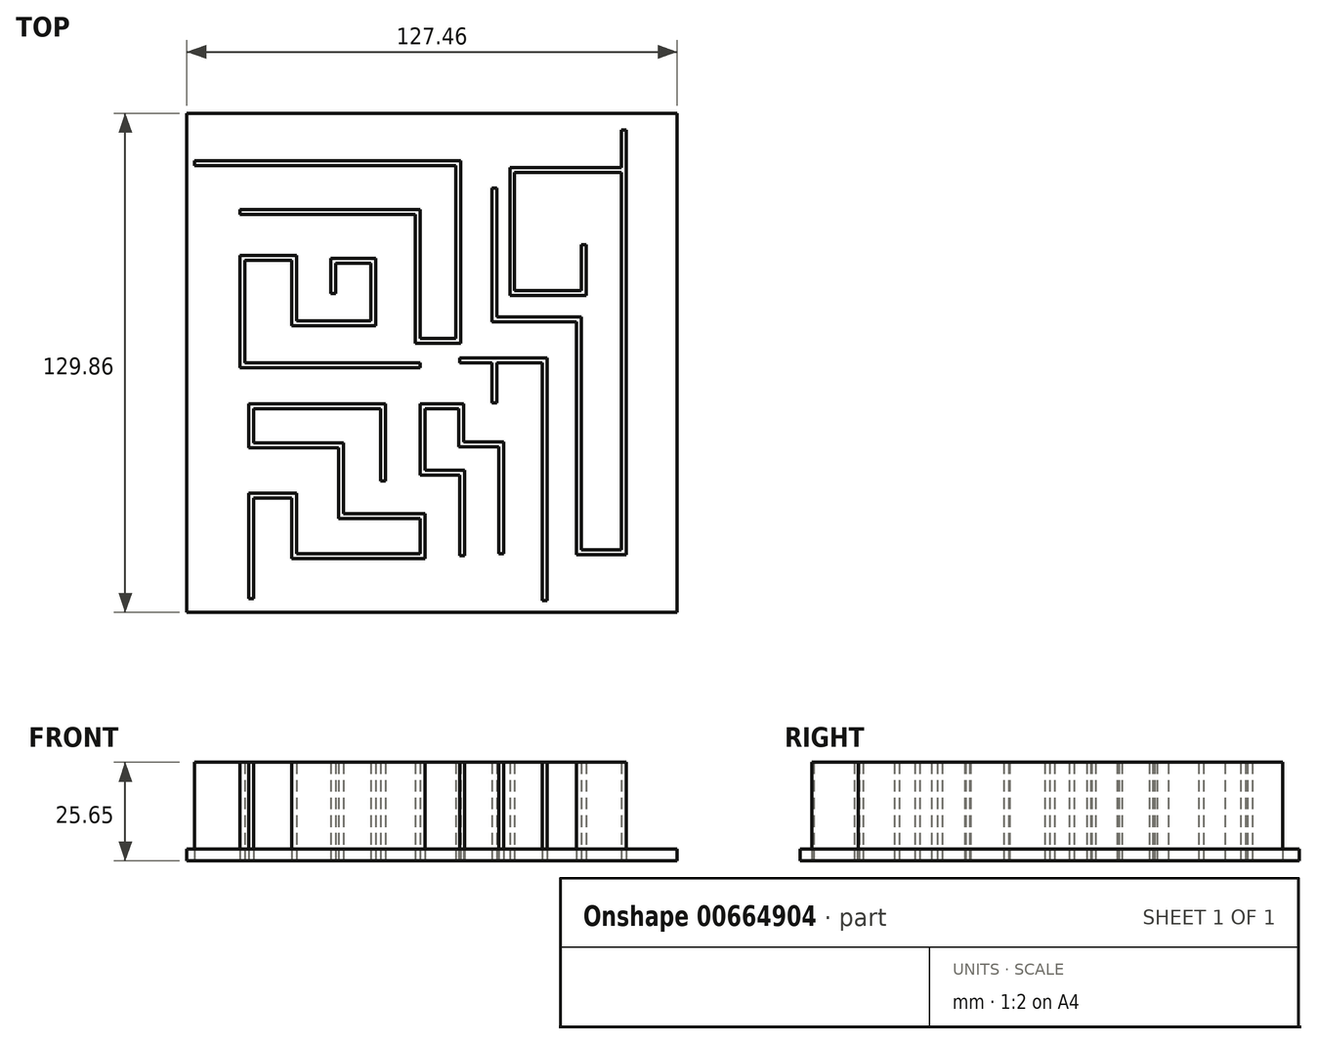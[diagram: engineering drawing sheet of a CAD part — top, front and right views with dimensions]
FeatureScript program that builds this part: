
annotation { "Feature Type Name" : "Feature", "Feature Type Description" : "" }
export const myFeature = defineFeature(function(context is Context, id is Id, definition is map)
    precondition{}
    {
        {
            var Q0;
            Q0=qCreatedBy(makeId("Top.planeOp"),FACE);
            var sketch = newSketch(context, id + "F0", { "sketchPlane" : qUnion([Q0])});
            skLineSegment(sketch, "E0", {"start": v(-44.65, -61.31) * mm, "end": v(-44.65, -33.84) * mm});
            skLineSegment(sketch, "E1", {"start": v(-44.65, -33.84) * mm, "end": v(-32.18, -33.84) * mm});
            skLineSegment(sketch, "E2", {"start": v(-32.18, -33.84) * mm, "end": v(-32.18, -49.6) * mm});
            skLineSegment(sketch, "E3", {"start": v(-32.18, -49.6) * mm, "end": v(0, -49.6) * mm});
            skLineSegment(sketch, "E4", {"start": v(0, -49.6) * mm, "end": v(0, -40.45) * mm});
            skLineSegment(sketch, "E5", {"start": v(0, -40.45) * mm, "end": v(-21.24, -40.45) * mm});
            skLineSegment(sketch, "E6", {"start": v(-21.24, -40.45) * mm, "end": v(-21.24, -22.13) * mm});
            skLineSegment(sketch, "E7", {"start": v(-21.24, -22.13) * mm, "end": v(-44.65, -22.13) * mm});
            skLineSegment(sketch, "E8", {"start": v(-44.65, -22.13) * mm, "end": v(-44.65, -10.68) * mm});
            skLineSegment(sketch, "E9", {"start": v(-44.65, -10.68) * mm, "end": v(-9.03, -10.68) * mm});
            skLineSegment(sketch, "E10", {"start": v(-9.03, -10.68) * mm, "end": v(-9.03, -30.78) * mm});
            skLineSegment(sketch, "E11", {"start": v(0, 0) * mm, "end": v(-45.67, 0) * mm});
            skLineSegment(sketch, "E12", {"start": v(-45.67, 0) * mm, "end": v(-45.67, 26.71) * mm});
            skLineSegment(sketch, "E13", {"start": v(-45.67, 26.71) * mm, "end": v(-33.45, 26.71) * mm});
            skLineSegment(sketch, "E14", {"start": v(-33.45, 26.71) * mm, "end": v(-33.45, 9.67) * mm});
            skLineSegment(sketch, "E15", {"start": v(-33.45, 9.67) * mm, "end": v(-11.58, 9.67) * mm});
            skLineSegment(sketch, "E16", {"start": v(-11.58, 9.67) * mm, "end": v(-11.58, 27.22) * mm});
            skLineSegment(sketch, "E17", {"start": v(-11.58, 27.22) * mm, "end": v(-23.28, 27.22) * mm});
            skLineSegment(sketch, "E18", {"start": v(-23.28, 27.22) * mm, "end": v(-23.28, 18.06) * mm});
            skLineSegment(sketch, "E19", {"start": v(0, 39.93) * mm, "end": v(0, 6.37) * mm});
            skLineSegment(sketch, "E20", {"start": v(0, 6.37) * mm, "end": v(9.29, 6.37) * mm});
            skLineSegment(sketch, "E21", {"start": v(9.29, 6.37) * mm, "end": v(9.29, 51.38) * mm});
            skLineSegment(sketch, "E22", {"start": v(9.29, 51.38) * mm, "end": v(-46.67, 51.38) * mm});
            skLineSegment(sketch, "E23", {"start": v(10.3, -50.12) * mm, "end": v(10.3, -29.26) * mm});
            skLineSegment(sketch, "E24", {"start": v(10.3, -29.26) * mm, "end": v(0, -29.26) * mm});
            skLineSegment(sketch, "E25", {"start": v(0, -29.26) * mm, "end": v(0, -10.68) * mm});
            skLineSegment(sketch, "E26", {"start": v(0, -10.68) * mm, "end": v(11.32, -10.68) * mm});
            skLineSegment(sketch, "E27", {"start": v(11.32, -10.68) * mm, "end": v(11.32, -20.6) * mm});
            skLineSegment(sketch, "E28", {"start": v(11.32, -20.6) * mm, "end": v(21.75, -20.6) * mm});
            skLineSegment(sketch, "E29", {"start": v(21.75, -20.6) * mm, "end": v(21.75, -49.6) * mm});
            skLineSegment(sketch, "E30", {"start": v(21.75, -49.6) * mm, "end": v(31.67, -49.6) * mm});
            skLineSegment(sketch, "E31", {"start": v(31.67, -49.6) * mm, "end": v(31.67, -10.44) * mm});
            skLineSegment(sketch, "E32", {"start": v(31.67, -10.44) * mm, "end": v(31.67, 0) * mm});
            skLineSegment(sketch, "E33", {"start": v(31.67, 0) * mm, "end": v(19.97, 0) * mm});
            skLineSegment(sketch, "E34", {"start": v(19.97, 0) * mm, "end": v(19.97, -10.44) * mm});
            skLineSegment(sketch, "E35", {"start": v(19.97, 0) * mm, "end": v(10.3, 0) * mm});
            skLineSegment(sketch, "E36", {"start": v(19.97, 45.54) * mm, "end": v(19.97, 11.96) * mm});
            skLineSegment(sketch, "E37", {"start": v(19.97, 11.96) * mm, "end": v(41.85, 11.96) * mm});
            skLineSegment(sketch, "E38", {"start": v(41.85, 11.96) * mm, "end": v(41.85, -48.6) * mm});
            skLineSegment(sketch, "E39", {"start": v(41.85, -48.6) * mm, "end": v(52.28, -48.6) * mm});
            skLineSegment(sketch, "E40", {"start": v(52.28, -48.6) * mm, "end": v(52.28, 49.6) * mm});
            skLineSegment(sketch, "E41", {"start": v(52.28, 49.6) * mm, "end": v(24.56, 49.6) * mm});
            skLineSegment(sketch, "E42", {"start": v(24.56, 49.6) * mm, "end": v(24.56, 18.83) * mm});
            skLineSegment(sketch, "E43", {"start": v(24.56, 18.83) * mm, "end": v(41.85, 18.83) * mm});
            skLineSegment(sketch, "E44", {"start": v(41.85, 18.83) * mm, "end": v(41.85, 30.8) * mm});
            skLineSegment(sketch, "E45", {"start": v(52.28, 49.6) * mm, "end": v(52.28, 60.55) * mm});
            skLineSegment(sketch, "E46", {"start": v(-46.67, 51.38) * mm, "end": v(-58.64, 51.38) * mm});
            skLineSegment(sketch, "E47", {"start": v(31.67, -49.6) * mm, "end": v(31.67, -61.82) * mm});
            skLineSegment(sketch, "E48.0", {"start": v(-10.3, -11.95) * mm, "end": v(-10.3, -30.78) * mm});
            skLineSegment(sketch, "E48.1", {"start": v(-33.45, -50.88) * mm, "end": v(1.27, -50.88) * mm});
            skLineSegment(sketch, "E48.2", {"start": v(-33.45, -35.1) * mm, "end": v(-33.45, -50.88) * mm});
            skLineSegment(sketch, "E48.3", {"start": v(-43.38, -35.1) * mm, "end": v(-33.45, -35.1) * mm});
            skLineSegment(sketch, "E48.4", {"start": v(-43.38, -61.31) * mm, "end": v(-43.38, -35.1) * mm});
            skLineSegment(sketch, "E48.5", {"start": v(1.27, -50.88) * mm, "end": v(1.27, -39.18) * mm});
            skLineSegment(sketch, "E48.6", {"start": v(1.27, -39.18) * mm, "end": v(-19.97, -39.18) * mm});
            skLineSegment(sketch, "E48.7", {"start": v(-19.97, -39.18) * mm, "end": v(-19.97, -20.86) * mm});
            skLineSegment(sketch, "E48.8", {"start": v(-19.97, -20.86) * mm, "end": v(-43.38, -20.86) * mm});
            skLineSegment(sketch, "E48.9", {"start": v(-43.38, -20.86) * mm, "end": v(-43.38, -11.95) * mm});
            skLineSegment(sketch, "E48.10", {"start": v(-43.38, -11.95) * mm, "end": v(-10.3, -11.95) * mm});
            skLineSegment(sketch, "E49.0", {"start": v(-22, 25.95) * mm, "end": v(-22, 18.06) * mm});
            skLineSegment(sketch, "E49.1", {"start": v(-12.85, 25.95) * mm, "end": v(-22, 25.95) * mm});
            skLineSegment(sketch, "E49.2", {"start": v(-12.85, 10.94) * mm, "end": v(-12.85, 25.95) * mm});
            skLineSegment(sketch, "E49.3", {"start": v(-32.18, 10.94) * mm, "end": v(-12.85, 10.94) * mm});
            skLineSegment(sketch, "E49.4", {"start": v(0, -1.27) * mm, "end": v(-46.94, -1.27) * mm});
            skLineSegment(sketch, "E49.5", {"start": v(-46.94, -1.27) * mm, "end": v(-46.94, 27.98) * mm});
            skLineSegment(sketch, "E49.6", {"start": v(-46.94, 27.98) * mm, "end": v(-32.18, 27.98) * mm});
            skLineSegment(sketch, "E49.7", {"start": v(-32.18, 27.98) * mm, "end": v(-32.18, 10.94) * mm});
            skLineSegment(sketch, "E50.0", {"start": v(-46.67, 52.65) * mm, "end": v(-58.64, 52.65) * mm});
            skLineSegment(sketch, "E50.1", {"start": v(10.56, 52.65) * mm, "end": v(-46.67, 52.65) * mm});
            skLineSegment(sketch, "E50.3", {"start": v(-1.27, 38.66) * mm, "end": v(-1.27, 5.1) * mm});
            skLineSegment(sketch, "E50.4", {"start": v(-1.27, 5.1) * mm, "end": v(10.56, 5.1) * mm});
            skLineSegment(sketch, "E50.5", {"start": v(10.56, 5.1) * mm, "end": v(10.56, 52.65) * mm});
            skLineSegment(sketch, "E51", {"start": v(-46.94, 39.93) * mm, "end": v(0, 39.93) * mm});
            skPoint(sketch, "E51.startSnap0", {"position": v(-46.94, 13.36) * mm});
            skLineSegment(sketch, "E52.0", {"start": v(-46.94, 38.66) * mm, "end": v(-1.27, 38.66) * mm});
            skLineSegment(sketch, "E53.0", {"start": v(-46.67, 52.27) * mm, "end": v(-58.64, 52.27) * mm});
            skLineSegment(sketch, "E53.1", {"start": v(-0.9, 32.07) * mm, "end": v(-0.9, 5.48) * mm});
            skLineSegment(sketch, "E53.2", {"start": v(-0.9, 5.48) * mm, "end": v(10.18, 5.48) * mm});
            skLineSegment(sketch, "E53.3", {"start": v(10.18, 5.48) * mm, "end": v(10.18, 52.27) * mm});
            skLineSegment(sketch, "E53.4", {"start": v(10.18, 52.27) * mm, "end": v(-46.67, 52.27) * mm});
            skLineSegment(sketch, "E54.0", {"start": v(20.48, -21.88) * mm, "end": v(20.48, -49.6) * mm});
            skLineSegment(sketch, "E54.1", {"start": v(10.05, -21.88) * mm, "end": v(20.48, -21.88) * mm});
            skLineSegment(sketch, "E54.2", {"start": v(10.05, -11.95) * mm, "end": v(10.05, -21.88) * mm});
            skLineSegment(sketch, "E54.3", {"start": v(11.57, -50.12) * mm, "end": v(11.57, -27.99) * mm});
            skLineSegment(sketch, "E54.4", {"start": v(11.57, -27.99) * mm, "end": v(1.27, -27.99) * mm});
            skLineSegment(sketch, "E54.5", {"start": v(1.27, -27.99) * mm, "end": v(1.27, -11.95) * mm});
            skLineSegment(sketch, "E54.6", {"start": v(1.27, -11.95) * mm, "end": v(10.05, -11.95) * mm});
            skLineSegment(sketch, "E55.0", {"start": v(18.7, 1.27) * mm, "end": v(18.7, -10.44) * mm});
            skLineSegment(sketch, "E55.1", {"start": v(32.94, 1.27) * mm, "end": v(18.7, 1.27) * mm});
            skLineSegment(sketch, "E55.2", {"start": v(32.94, -10.44) * mm, "end": v(32.94, 1.27) * mm});
            skLineSegment(sketch, "E56.0", {"start": v(19.97, 1.27) * mm, "end": v(10.3, 1.27) * mm});
            skLineSegment(sketch, "E57.0", {"start": v(32.94, -49.6) * mm, "end": v(32.94, -10.44) * mm});
            skLineSegment(sketch, "E57.1", {"start": v(32.94, -49.6) * mm, "end": v(32.94, -61.82) * mm});
            skLineSegment(sketch, "E58.0", {"start": v(53.55, 44.52) * mm, "end": v(53.55, 60.55) * mm});
            skLineSegment(sketch, "E58.1", {"start": v(53.55, -49.86) * mm, "end": v(53.55, 44.52) * mm});
            skLineSegment(sketch, "E58.2", {"start": v(18.7, 45.54) * mm, "end": v(18.7, 10.69) * mm});
            skLineSegment(sketch, "E58.3", {"start": v(18.7, 10.69) * mm, "end": v(40.58, 10.69) * mm});
            skLineSegment(sketch, "E58.4", {"start": v(40.58, 10.69) * mm, "end": v(40.58, -49.86) * mm});
            skLineSegment(sketch, "E58.5", {"start": v(40.58, -49.86) * mm, "end": v(53.55, -49.86) * mm});
            skLineSegment(sketch, "E59.0", {"start": v(43.12, 17.56) * mm, "end": v(43.12, 30.8) * mm});
            skLineSegment(sketch, "E59.1", {"start": v(23.29, 17.56) * mm, "end": v(43.12, 17.56) * mm});
            skLineSegment(sketch, "E59.2", {"start": v(23.29, 50.87) * mm, "end": v(23.29, 17.56) * mm});
            skLineSegment(sketch, "E59.3", {"start": v(52.28, 50.87) * mm, "end": v(23.29, 50.87) * mm});
            skLineSegment(sketch, "E60", {"start": v(-44.65, -61.31) * mm, "end": v(-43.38, -61.31) * mm});
            skLineSegment(sketch, "E61", {"start": v(-10.3, -30.78) * mm, "end": v(-9.03, -30.78) * mm});
            skLineSegment(sketch, "E62", {"start": v(10.3, -50.12) * mm, "end": v(11.57, -50.12) * mm});
            skLineSegment(sketch, "E63", {"start": v(20.48, -49.6) * mm, "end": v(21.75, -49.6) * mm});
            skLineSegment(sketch, "E64", {"start": v(31.67, -61.82) * mm, "end": v(32.94, -61.82) * mm});
            skLineSegment(sketch, "E65", {"start": v(18.7, -10.44) * mm, "end": v(19.97, -10.44) * mm});
            skLineSegment(sketch, "E66", {"start": v(10.3, 0) * mm, "end": v(10.3, 1.27) * mm});
            skLineSegment(sketch, "E67", {"start": v(-58.64, 51.38) * mm, "end": v(-58.64, 52.65) * mm});
            skLineSegment(sketch, "E68", {"start": v(-46.94, 38.66) * mm, "end": v(-46.94, 39.93) * mm});
            skLineSegment(sketch, "E69", {"start": v(-23.28, 18.06) * mm, "end": v(-22, 18.06) * mm});
            skLineSegment(sketch, "E70", {"start": v(0, 0) * mm, "end": v(0, -1.27) * mm});
            skLineSegment(sketch, "E71", {"start": v(18.7, 45.54) * mm, "end": v(19.97, 45.54) * mm});
            skLineSegment(sketch, "E72", {"start": v(41.85, 30.8) * mm, "end": v(43.12, 30.8) * mm});
            skLineSegment(sketch, "E73", {"start": v(52.28, 60.55) * mm, "end": v(53.55, 60.55) * mm});
            skSolve(sketch);
        }
        {
            var Q0;
            Q0 = qSketchRegion(id + "F0", true);
            extrude(context, id + "F1", {"entities" : qUnion([Q0]), "depth" : 25.65 * mm, "offsetDistance" : 25.4 * mm});
        }
        {
            var Q0;
            Q0=qCreatedBy(makeId("Top.planeOp"),FACE);
            var sketch = newSketch(context, id + "F2", { "sketchPlane" : qUnion([Q0])});
            skLineSegment(sketch, "E74.bottom", {"start": v(-60.67, 64.94) * mm, "end": v(66.79, 64.94) * mm});
            skLineSegment(sketch, "E74.top", {"start": v(-60.67, -64.92) * mm, "end": v(66.79, -64.92) * mm});
            skLineSegment(sketch, "E74.left", {"start": v(-60.67, 64.94) * mm, "end": v(-60.67, -64.92) * mm});
            skLineSegment(sketch, "E74.right", {"start": v(66.79, 64.94) * mm, "end": v(66.79, -64.92) * mm});
            skSolve(sketch);
        }
        {
            var Q0;
            Q0 = qSketchRegion(id + "F2", true);
            extrude(context, id + "F3", {"entities" : qUnion([Q0]), "depth" : 3.05 * mm, "offsetDistance" : 25.4 * mm});
        }
        {
            var Q0;
            Q0=qCreatedBy(makeId("Top.planeOp"),FACE);
            var sketch = newSketch(context, id + "F4", { "sketchPlane" : qUnion([Q0])});
            skLineSegment(sketch, "E75.bottom", {"start": v(-60.93, 65.64) * mm, "end": v(66.27, 65.64) * mm});
            skLineSegment(sketch, "E75.top", {"start": v(-60.93, -64.87) * mm, "end": v(66.27, -64.87) * mm});
            skLineSegment(sketch, "E75.left", {"start": v(-60.93, 65.64) * mm, "end": v(-60.93, -64.87) * mm});
            skLineSegment(sketch, "E75.right", {"start": v(66.27, 65.64) * mm, "end": v(66.27, -64.87) * mm});
            skLineSegment(sketch, "E76.0", {"start": v(-59.66, 64.37) * mm, "end": v(65, 64.37) * mm});
            skLineSegment(sketch, "E76.1", {"start": v(-59.66, 64.37) * mm, "end": v(-59.66, -63.6) * mm});
            skLineSegment(sketch, "E76.2", {"start": v(-59.66, -63.6) * mm, "end": v(65, -63.6) * mm});
            skLineSegment(sketch, "E76.3", {"start": v(65, 64.37) * mm, "end": v(65, -63.6) * mm});
            skSolve(sketch);
        }
        {
            var Q0;
            Q0 = qConstructionFilter(qBodyType(qCreatedBy(id + "F4" ,EDGE), BodyType.WIRE), ConstructionObject.NO);
            extrude(context, id + "F5", {"bodyType" : ToolBodyType.SURFACE, "surfaceEntities" : qUnion([Q0]), "depth" : 25.4 * mm, "offsetDistance" : 25.4 * mm});
        }
    });
